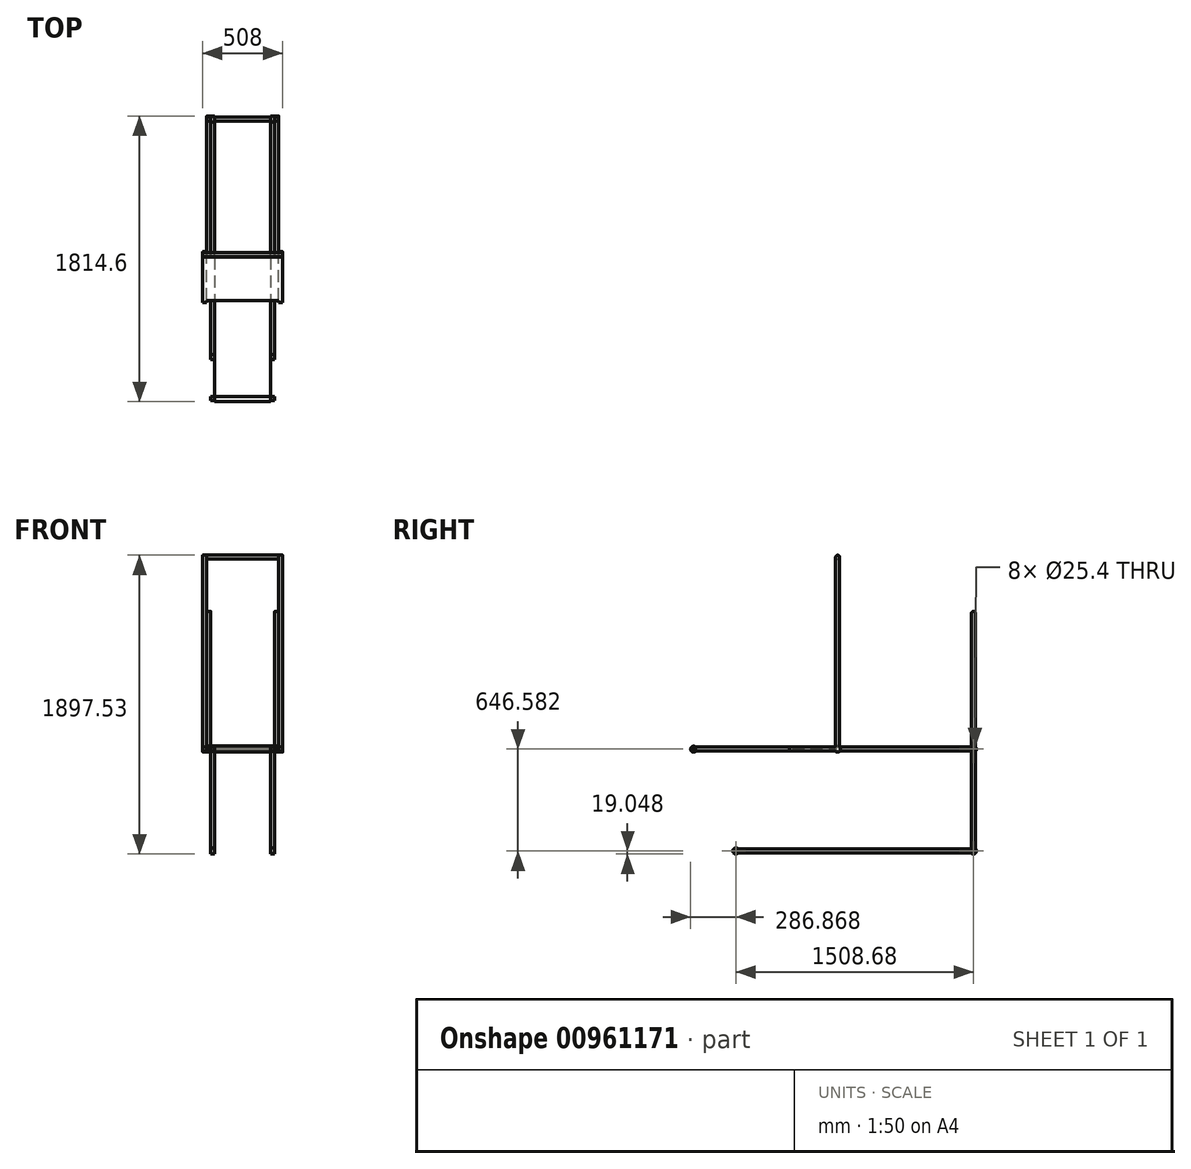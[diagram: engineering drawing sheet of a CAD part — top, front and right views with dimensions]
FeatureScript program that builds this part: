
annotation { "Feature Type Name" : "Feature", "Feature Type Description" : "" }
export const myFeature = defineFeature(function(context is Context, id is Id, definition is map)
    precondition{}
    {
        {
            var Q0;
            Q0=qCreatedBy(makeId("Right.planeOp"),FACE);
            var sketch = newSketch(context, id + "F0", { "sketchPlane" : qUnion([Q0])});
            skCircle(sketch, "E0", {"center": v(0, 0) * mm, "radius": 12.7 * mm});
            skLineSegment(sketch, "E1", {"start": v(12.7, 0) * mm, "end": v(12.7, 1219.2) * mm});
            skLineSegment(sketch, "E2", {"start": v(-12.7, 0) * mm, "end": v(-12.7, 1219.2) * mm});
            skLineSegment(sketch, "E3", {"start": v(0, -12.7) * mm, "end": v(-304.8, -12.7) * mm});
            skLineSegment(sketch, "E4", {"start": v(0, 12.7) * mm, "end": v(-304.8, 12.7) * mm});
            skLineSegment(sketch, "E5", {"start": v(-304.8, -12.7) * mm, "end": v(-304.8, 12.7) * mm});
            skLineSegment(sketch, "E6", {"start": v(-12.7, 1219.2) * mm, "end": v(12.7, 1219.2) * mm});
            skLineSegment(sketch, "E7", {"start": v(-304.8, 12.7) * mm, "end": v(-914.4, 12.7) * mm});
            skLineSegment(sketch, "E8", {"start": v(-304.8, -12.7) * mm, "end": v(-914.4, -12.7) * mm});
            skLineSegment(sketch, "E9", {"start": v(-914.4, -12.7) * mm, "end": v(-914.4, 12.7) * mm});
            skCircle(sketch, "E10", {"center": v(862.1, 0) * mm, "radius": 12.7 * mm});
            skLineSegment(sketch, "E11", {"start": v(0, -12.7) * mm, "end": v(862.1, -12.7) * mm});
            skLineSegment(sketch, "E12", {"start": v(862.1, 12.7) * mm, "end": v(0, 12.7) * mm});
            skLineSegment(sketch, "E13", {"start": v(874.8, 0) * mm, "end": v(874.8, 862.1) * mm});
            skLineSegment(sketch, "E14", {"start": v(849.4, 0) * mm, "end": v(849.4, 862.1) * mm});
            skCircle(sketch, "E15", {"center": v(-914.4, 0) * mm, "radius": 12.7 * mm});
            skLineSegment(sketch, "E16", {"start": v(849.4, 862.1) * mm, "end": v(874.8, 862.1) * mm});
            skCircle(sketch, "E17", {"center": v(862.1, 862.1) * mm, "radius": 12.7 * mm});
            skCircle(sketch, "E18", {"center": v(862.1, -646.58) * mm, "radius": 12.7 * mm});
            skLineSegment(sketch, "E19", {"start": v(849.4, -646.58) * mm, "end": v(849.4, 0) * mm});
            skLineSegment(sketch, "E20", {"start": v(874.8, -646.58) * mm, "end": v(874.8, 0) * mm});
            skCircle(sketch, "E21", {"center": v(-646.58, -646.58) * mm, "radius": 12.7 * mm});
            skLineSegment(sketch, "E22", {"start": v(-646.58, -659.28) * mm, "end": v(862.1, -659.28) * mm});
            skLineSegment(sketch, "E23", {"start": v(-646.58, -633.88) * mm, "end": v(862.1, -633.88) * mm});
            skCircle(sketch, "E24", {"center": v(0, 1219.2) * mm, "radius": 12.7 * mm});
            skCircle(sketch, "E25", {"center": v(0, 0) * mm, "radius": 19.05 * mm});
            skCircle(sketch, "E26", {"center": v(862.1, 0) * mm, "radius": 19.05 * mm});
            skCircle(sketch, "E27", {"center": v(862.1, -646.58) * mm, "radius": 19.05 * mm});
            skCircle(sketch, "E28", {"center": v(-914.4, 0) * mm, "radius": 19.05 * mm});
            skCircle(sketch, "E29", {"center": v(-646.58, -646.58) * mm, "radius": 19.05 * mm});
            skCircle(sketch, "E30", {"center": v(-304.8, 0) * mm, "radius": 12.7 * mm});
            skCircle(sketch, "E31", {"center": v(-304.8, 0) * mm, "radius": 19.05 * mm});
            skLineSegment(sketch, "E32.0", {"start": v(-17.96, -6.35) * mm, "end": v(-932.36, -6.35) * mm});
            skLineSegment(sketch, "E33.trimOffspring", {"start": v(-17.96, 6.35) * mm, "end": v(-932.36, 6.35) * mm});
            skSolve(sketch);
        }
        {
            var Q0;
            {var subQ1=sQuery(id+"F0.wireOp",EDGE,"E3");var subQ3=sQuery(id+"F0.wireOp",EDGE,"E25");var subQ4=makeQuery(id+"F0.imprint","INTERSECT",VERTEX,{"derivedFrom":[subQ1,subQ3]});Q0=makeQuery(id+"F0.imprint","IMPRINT",FACE,{"disambiguationData":[TD([[makeQuery(id+"F0.imprint","IMPRINT",EDGE,{"disambiguationData":[TD([[subQ4,-1.0]])],"derivedFrom":subQ3}),1.0]])]});}
            var Q1;
            {var subQ0=sQuery(id+"F0.wireOp",EDGE,"E6");Q1=makeQuery(id+"F0.imprint","IMPRINT",FACE,{"disambiguationData":[TD([[makeQuery(id+"F0.imprint","IMPRINT",EDGE,{"derivedFrom":subQ0}),-1.0]])]});}
            var Q2;
            {var subQ0=sQuery(id+"F0.wireOp",EDGE,"E2");var subQ1=sQuery(id+"F0.wireOp",EDGE,"E0");var subQ2=makeQuery(id+"F0.imprint","INTERSECT",VERTEX,{"derivedFrom":[subQ1,subQ0]});Q2=makeQuery(id+"F0.imprint","IMPRINT",FACE,{"disambiguationData":[TD([[makeQuery(id+"F0.imprint","IMPRINT",EDGE,{"disambiguationData":[TD([[subQ2,-1.0]])],"derivedFrom":subQ0}),-1.0]])]});}
            var Q3;
            {var subQ0=sQuery(id+"F0.wireOp",EDGE,"E1");var subQ1=sQuery(id+"F0.wireOp",EDGE,"E0");var subQ2=makeQuery(id+"F0.imprint","INTERSECT",VERTEX,{"derivedFrom":[subQ1,subQ0]});Q3=makeQuery(id+"F0.imprint","IMPRINT",FACE,{"disambiguationData":[TD([[makeQuery(id+"F0.imprint","IMPRINT",EDGE,{"disambiguationData":[TD([[subQ2,-1.0]])],"derivedFrom":subQ0}),1.0]])]});}
            var Q4;
            {var subQ3=sQuery(id+"F0.wireOp",EDGE,"E1");var subQ6=sQuery(id+"F0.wireOp",EDGE,"E0");var subQ9=makeQuery(id+"F0.imprint","INTERSECT",VERTEX,{"derivedFrom":[subQ6,subQ3]});Q4=makeQuery(id+"F0.imprint","IMPRINT",FACE,{"disambiguationData":[TD([[makeQuery(id+"F0.imprint","IMPRINT",EDGE,{"disambiguationData":[TD([[subQ9,-1.0]])],"derivedFrom":subQ3}),-1.0]])]});}
            var Q5;
            {var subQ0=sQuery(id+"F0.wireOp",EDGE,"E6");Q5=makeQuery(id+"F0.imprint","IMPRINT",FACE,{"disambiguationData":[TD([[makeQuery(id+"F0.imprint","IMPRINT",EDGE,{"derivedFrom":subQ0}),1.0]])]});}
            var Q6;
            {var subQ5=sQuery(id+"F0.wireOp",EDGE,"E25");var subQ7=sQuery(id+"F0.wireOp",EDGE,"E1");var subQ9=makeQuery(id+"F0.imprint","INTERSECT",VERTEX,{"derivedFrom":[subQ7,subQ5]});Q6=makeQuery(id+"F0.imprint","IMPRINT",FACE,{"disambiguationData":[TD([[makeQuery(id+"F0.imprint","IMPRINT",EDGE,{"disambiguationData":[TD([[subQ9,1.0]])],"derivedFrom":subQ7}),1.0]])]});}
            var Q7;
            {var subQ2=sQuery(id+"F0.wireOp",EDGE,"E1");var subQ4=sQuery(id+"F0.wireOp",EDGE,"E25");var subQ5=makeQuery(id+"F0.imprint","INTERSECT",VERTEX,{"derivedFrom":[subQ2,subQ4]});Q7=makeQuery(id+"F0.imprint","IMPRINT",FACE,{"disambiguationData":[TD([[makeQuery(id+"F0.imprint","IMPRINT",EDGE,{"disambiguationData":[TD([[subQ5,-1.0]])],"derivedFrom":subQ4}),-1.0]])]});}
            var Q8;
            {var subQ3=sQuery(id+"F0.wireOp",EDGE,"E2");var subQ5=sQuery(id+"F0.wireOp",EDGE,"E0");var subQ6=makeQuery(id+"F0.imprint","INTERSECT",VERTEX,{"derivedFrom":[subQ5,subQ3]});Q8=makeQuery(id+"F0.imprint","IMPRINT",FACE,{"disambiguationData":[TD([[makeQuery(id+"F0.imprint","IMPRINT",EDGE,{"disambiguationData":[TD([[subQ6,-1.0]])],"derivedFrom":subQ3}),1.0]])]});}
            var Q9;
            {var subQ0=sQuery(id+"F0.wireOp",EDGE,"E25");var subQ1=sQuery(id+"F0.wireOp",EDGE,"E1");var subQ2=makeQuery(id+"F0.imprint","INTERSECT",VERTEX,{"derivedFrom":[subQ1,subQ0]});Q9=makeQuery(id+"F0.imprint","IMPRINT",FACE,{"disambiguationData":[TD([[makeQuery(id+"F0.imprint","IMPRINT",EDGE,{"disambiguationData":[TD([[subQ2,1.0]])],"derivedFrom":subQ1}),-1.0]])]});}
            var Q10;
            {var subQ0=sQuery(id+"F0.wireOp",EDGE,"E25");var subQ1=sQuery(id+"F0.wireOp",EDGE,"E2");var subQ2=makeQuery(id+"F0.imprint","INTERSECT",VERTEX,{"derivedFrom":[subQ1,subQ0]});Q10=makeQuery(id+"F0.imprint","IMPRINT",FACE,{"disambiguationData":[TD([[makeQuery(id+"F0.imprint","IMPRINT",EDGE,{"disambiguationData":[TD([[subQ2,1.0]])],"derivedFrom":subQ1}),1.0]])]});}
            var Q11;
            {var subQ0=sQuery(id+"F0.wireOp",EDGE,"E25");var subQ1=sQuery(id+"F0.wireOp",EDGE,"E3");var subQ2=makeQuery(id+"F0.imprint","INTERSECT",VERTEX,{"derivedFrom":[subQ1,subQ0]});Q11=makeQuery(id+"F0.imprint","IMPRINT",FACE,{"disambiguationData":[TD([[makeQuery(id+"F0.imprint","IMPRINT",EDGE,{"disambiguationData":[TD([[subQ2,-1.0]])],"derivedFrom":subQ1}),-1.0]])]});}
            var Q12;
            {var subQ2=sQuery(id+"F0.wireOp",EDGE,"E3");var subQ4=sQuery(id+"F0.wireOp",EDGE,"E31");var subQ5=makeQuery(id+"F0.imprint","INTERSECT",VERTEX,{"derivedFrom":[subQ2,subQ4]});Q12=makeQuery(id+"F0.imprint","IMPRINT",FACE,{"disambiguationData":[TD([[makeQuery(id+"F0.imprint","IMPRINT",EDGE,{"disambiguationData":[TD([[subQ5,-1.0]])],"derivedFrom":subQ4}),1.0]])]});}
            var Q13;
            {var subQ1=sQuery(id+"F0.wireOp",EDGE,"E4");var subQ3=sQuery(id+"F0.wireOp",EDGE,"E31");var subQ4=makeQuery(id+"F0.imprint","INTERSECT",VERTEX,{"derivedFrom":[subQ1,subQ3]});Q13=makeQuery(id+"F0.imprint","IMPRINT",FACE,{"disambiguationData":[TD([[makeQuery(id+"F0.imprint","IMPRINT",EDGE,{"disambiguationData":[TD([[subQ4,1.0]])],"derivedFrom":subQ3}),1.0]])]});}
            var Q14;
            {var subQ0=sQuery(id+"F0.wireOp",EDGE,"E25");var subQ1=sQuery(id+"F0.wireOp",EDGE,"E4");var subQ2=makeQuery(id+"F0.imprint","INTERSECT",VERTEX,{"derivedFrom":[subQ1,subQ0]});Q14=makeQuery(id+"F0.imprint","IMPRINT",FACE,{"disambiguationData":[TD([[makeQuery(id+"F0.imprint","IMPRINT",EDGE,{"disambiguationData":[TD([[subQ2,-1.0]])],"derivedFrom":subQ1}),1.0]])]});}
            var Q15;
            {var subQ1=sQuery(id+"F0.wireOp",EDGE,"E5");var subQ3=sQuery(id+"F0.wireOp",EDGE,"E33.trimOffspring");var subQ4=makeQuery(id+"F0.imprint","INTERSECT",VERTEX,{"derivedFrom":[subQ1,subQ3]});Q15=makeQuery(id+"F0.imprint","IMPRINT",FACE,{"disambiguationData":[TD([[makeQuery(id+"F0.imprint","IMPRINT",EDGE,{"disambiguationData":[TD([[subQ4,1.0]])],"derivedFrom":subQ3}),-1.0]])]});}
            var Q16;
            {var subQ1=sQuery(id+"F0.wireOp",EDGE,"E5");var subQ3=sQuery(id+"F0.wireOp",EDGE,"E32.0");var subQ4=makeQuery(id+"F0.imprint","INTERSECT",VERTEX,{"derivedFrom":[subQ1,subQ3]});Q16=makeQuery(id+"F0.imprint","IMPRINT",FACE,{"disambiguationData":[TD([[makeQuery(id+"F0.imprint","IMPRINT",EDGE,{"disambiguationData":[TD([[subQ4,1.0]])],"derivedFrom":subQ3}),1.0]])]});}
            var Q17;
            {var subQ0=sQuery(id+"F0.wireOp",EDGE,"E32.0");var subQ1=sQuery(id+"F0.wireOp",EDGE,"E5");var subQ2=makeQuery(id+"F0.imprint","INTERSECT",VERTEX,{"derivedFrom":[subQ1,subQ0]});Q17=makeQuery(id+"F0.imprint","IMPRINT",FACE,{"disambiguationData":[TD([[makeQuery(id+"F0.imprint","IMPRINT",EDGE,{"disambiguationData":[TD([[subQ2,-1.0]])],"derivedFrom":subQ1}),-1.0]])]});}
            var Q18;
            {var subQ0=sQuery(id+"F0.wireOp",EDGE,"E32.0");var subQ1=sQuery(id+"F0.wireOp",EDGE,"E25");var subQ2=makeQuery(id+"F0.imprint","INTERSECT",VERTEX,{"derivedFrom":[subQ1,subQ0]});Q18=makeQuery(id+"F0.imprint","IMPRINT",FACE,{"disambiguationData":[TD([[makeQuery(id+"F0.imprint","IMPRINT",EDGE,{"disambiguationData":[TD([[subQ2,1.0]])],"derivedFrom":subQ1}),-1.0]])]});}
            var Q19;
            {var subQ0=sQuery(id+"F0.wireOp",EDGE,"E33.trimOffspring");var subQ1=sQuery(id+"F0.wireOp",EDGE,"E30");var subQ2=makeQuery(id+"F0.imprint","INTERSECT",VERTEX,{"disambiguationData":[OD(0.0)],"derivedFrom":[subQ1,subQ0]});Q19=makeQuery(id+"F0.imprint","IMPRINT",FACE,{"disambiguationData":[TD([[makeQuery(id+"F0.imprint","IMPRINT",EDGE,{"disambiguationData":[TD([[subQ2,1.0]])],"derivedFrom":subQ1}),-1.0]])]});}
            extrude(context, id + "F1", {"entities" : qUnion([Q0, Q1, Q2, Q3, Q4, Q5, Q6, Q7, Q8, Q9, Q10, Q11, Q12, Q13, Q14, Q15, Q16, Q17, Q18, Q19]), "depth" : 254 * mm, "offsetDistance" : 25.4 * mm, "hasSecondDirection" : true, "secondDirectionOppositeDirection" : false, "secondDirectionDepth" : 228.6 * mm});
        }
        {
            var Q0;
            {var subQ0=sQuery(id+"F0.wireOp",EDGE,"E6");Q0=makeQuery(id+"F0.imprint","IMPRINT",FACE,{"disambiguationData":[TD([[makeQuery(id+"F0.imprint","IMPRINT",EDGE,{"derivedFrom":subQ0}),-1.0]])]});}
            var Q1;
            {var subQ5=sQuery(id+"F0.wireOp",EDGE,"E25");var subQ7=sQuery(id+"F0.wireOp",EDGE,"E1");var subQ9=makeQuery(id+"F0.imprint","INTERSECT",VERTEX,{"derivedFrom":[subQ7,subQ5]});Q1=makeQuery(id+"F0.imprint","IMPRINT",FACE,{"disambiguationData":[TD([[makeQuery(id+"F0.imprint","IMPRINT",EDGE,{"disambiguationData":[TD([[subQ9,1.0]])],"derivedFrom":subQ7}),1.0]])]});}
            var Q2;
            {var subQ3=sQuery(id+"F0.wireOp",EDGE,"E2");var subQ5=sQuery(id+"F0.wireOp",EDGE,"E0");var subQ6=makeQuery(id+"F0.imprint","INTERSECT",VERTEX,{"derivedFrom":[subQ5,subQ3]});Q2=makeQuery(id+"F0.imprint","IMPRINT",FACE,{"disambiguationData":[TD([[makeQuery(id+"F0.imprint","IMPRINT",EDGE,{"disambiguationData":[TD([[subQ6,-1.0]])],"derivedFrom":subQ3}),1.0]])]});}
            var Q3;
            {var subQ0=sQuery(id+"F0.wireOp",EDGE,"E1");var subQ1=sQuery(id+"F0.wireOp",EDGE,"E0");var subQ2=makeQuery(id+"F0.imprint","INTERSECT",VERTEX,{"derivedFrom":[subQ1,subQ0]});Q3=makeQuery(id+"F0.imprint","IMPRINT",FACE,{"disambiguationData":[TD([[makeQuery(id+"F0.imprint","IMPRINT",EDGE,{"disambiguationData":[TD([[subQ2,-1.0]])],"derivedFrom":subQ0}),1.0]])]});}
            var Q4;
            {var subQ0=sQuery(id+"F0.wireOp",EDGE,"E6");Q4=makeQuery(id+"F0.imprint","IMPRINT",FACE,{"disambiguationData":[TD([[makeQuery(id+"F0.imprint","IMPRINT",EDGE,{"derivedFrom":subQ0}),1.0]])]});}
            var Q5;
            {var subQ3=sQuery(id+"F0.wireOp",EDGE,"E1");var subQ6=sQuery(id+"F0.wireOp",EDGE,"E0");var subQ9=makeQuery(id+"F0.imprint","INTERSECT",VERTEX,{"derivedFrom":[subQ6,subQ3]});Q5=makeQuery(id+"F0.imprint","IMPRINT",FACE,{"disambiguationData":[TD([[makeQuery(id+"F0.imprint","IMPRINT",EDGE,{"disambiguationData":[TD([[subQ9,-1.0]])],"derivedFrom":subQ3}),-1.0]])]});}
            var Q6;
            {var subQ2=sQuery(id+"F0.wireOp",EDGE,"E1");var subQ4=sQuery(id+"F0.wireOp",EDGE,"E25");var subQ5=makeQuery(id+"F0.imprint","INTERSECT",VERTEX,{"derivedFrom":[subQ2,subQ4]});Q6=makeQuery(id+"F0.imprint","IMPRINT",FACE,{"disambiguationData":[TD([[makeQuery(id+"F0.imprint","IMPRINT",EDGE,{"disambiguationData":[TD([[subQ5,-1.0]])],"derivedFrom":subQ4}),-1.0]])]});}
            var Q7;
            {var subQ0=sQuery(id+"F0.wireOp",EDGE,"E25");var subQ1=sQuery(id+"F0.wireOp",EDGE,"E1");var subQ2=makeQuery(id+"F0.imprint","INTERSECT",VERTEX,{"derivedFrom":[subQ1,subQ0]});Q7=makeQuery(id+"F0.imprint","IMPRINT",FACE,{"disambiguationData":[TD([[makeQuery(id+"F0.imprint","IMPRINT",EDGE,{"disambiguationData":[TD([[subQ2,1.0]])],"derivedFrom":subQ1}),-1.0]])]});}
            var Q8;
            {var subQ0=sQuery(id+"F0.wireOp",EDGE,"E2");var subQ1=sQuery(id+"F0.wireOp",EDGE,"E0");var subQ2=makeQuery(id+"F0.imprint","INTERSECT",VERTEX,{"derivedFrom":[subQ1,subQ0]});Q8=makeQuery(id+"F0.imprint","IMPRINT",FACE,{"disambiguationData":[TD([[makeQuery(id+"F0.imprint","IMPRINT",EDGE,{"disambiguationData":[TD([[subQ2,-1.0]])],"derivedFrom":subQ0}),-1.0]])]});}
            var Q9;
            {var subQ1=sQuery(id+"F0.wireOp",EDGE,"E3");var subQ3=sQuery(id+"F0.wireOp",EDGE,"E25");var subQ4=makeQuery(id+"F0.imprint","INTERSECT",VERTEX,{"derivedFrom":[subQ1,subQ3]});Q9=makeQuery(id+"F0.imprint","IMPRINT",FACE,{"disambiguationData":[TD([[makeQuery(id+"F0.imprint","IMPRINT",EDGE,{"disambiguationData":[TD([[subQ4,-1.0]])],"derivedFrom":subQ3}),1.0]])]});}
            var Q10;
            {var subQ0=sQuery(id+"F0.wireOp",EDGE,"E25");var subQ1=sQuery(id+"F0.wireOp",EDGE,"E2");var subQ2=makeQuery(id+"F0.imprint","INTERSECT",VERTEX,{"derivedFrom":[subQ1,subQ0]});Q10=makeQuery(id+"F0.imprint","IMPRINT",FACE,{"disambiguationData":[TD([[makeQuery(id+"F0.imprint","IMPRINT",EDGE,{"disambiguationData":[TD([[subQ2,1.0]])],"derivedFrom":subQ1}),1.0]])]});}
            var Q11;
            {var subQ0=sQuery(id+"F0.wireOp",EDGE,"E25");var subQ1=sQuery(id+"F0.wireOp",EDGE,"E3");var subQ2=makeQuery(id+"F0.imprint","INTERSECT",VERTEX,{"derivedFrom":[subQ1,subQ0]});Q11=makeQuery(id+"F0.imprint","IMPRINT",FACE,{"disambiguationData":[TD([[makeQuery(id+"F0.imprint","IMPRINT",EDGE,{"disambiguationData":[TD([[subQ2,-1.0]])],"derivedFrom":subQ1}),-1.0]])]});}
            var Q12;
            {var subQ2=sQuery(id+"F0.wireOp",EDGE,"E3");var subQ4=sQuery(id+"F0.wireOp",EDGE,"E31");var subQ5=makeQuery(id+"F0.imprint","INTERSECT",VERTEX,{"derivedFrom":[subQ2,subQ4]});Q12=makeQuery(id+"F0.imprint","IMPRINT",FACE,{"disambiguationData":[TD([[makeQuery(id+"F0.imprint","IMPRINT",EDGE,{"disambiguationData":[TD([[subQ5,-1.0]])],"derivedFrom":subQ4}),1.0]])]});}
            var Q13;
            {var subQ0=sQuery(id+"F0.wireOp",EDGE,"E25");var subQ1=sQuery(id+"F0.wireOp",EDGE,"E4");var subQ2=makeQuery(id+"F0.imprint","INTERSECT",VERTEX,{"derivedFrom":[subQ1,subQ0]});Q13=makeQuery(id+"F0.imprint","IMPRINT",FACE,{"disambiguationData":[TD([[makeQuery(id+"F0.imprint","IMPRINT",EDGE,{"disambiguationData":[TD([[subQ2,-1.0]])],"derivedFrom":subQ1}),1.0]])]});}
            var Q14;
            {var subQ1=sQuery(id+"F0.wireOp",EDGE,"E4");var subQ3=sQuery(id+"F0.wireOp",EDGE,"E31");var subQ4=makeQuery(id+"F0.imprint","INTERSECT",VERTEX,{"derivedFrom":[subQ1,subQ3]});Q14=makeQuery(id+"F0.imprint","IMPRINT",FACE,{"disambiguationData":[TD([[makeQuery(id+"F0.imprint","IMPRINT",EDGE,{"disambiguationData":[TD([[subQ4,1.0]])],"derivedFrom":subQ3}),1.0]])]});}
            var Q15;
            {var subQ1=sQuery(id+"F0.wireOp",EDGE,"E5");var subQ3=sQuery(id+"F0.wireOp",EDGE,"E33.trimOffspring");var subQ4=makeQuery(id+"F0.imprint","INTERSECT",VERTEX,{"derivedFrom":[subQ1,subQ3]});Q15=makeQuery(id+"F0.imprint","IMPRINT",FACE,{"disambiguationData":[TD([[makeQuery(id+"F0.imprint","IMPRINT",EDGE,{"disambiguationData":[TD([[subQ4,1.0]])],"derivedFrom":subQ3}),-1.0]])]});}
            var Q16;
            {var subQ0=sQuery(id+"F0.wireOp",EDGE,"E32.0");var subQ1=sQuery(id+"F0.wireOp",EDGE,"E5");var subQ2=makeQuery(id+"F0.imprint","INTERSECT",VERTEX,{"derivedFrom":[subQ1,subQ0]});Q16=makeQuery(id+"F0.imprint","IMPRINT",FACE,{"disambiguationData":[TD([[makeQuery(id+"F0.imprint","IMPRINT",EDGE,{"disambiguationData":[TD([[subQ2,-1.0]])],"derivedFrom":subQ1}),-1.0]])]});}
            var Q17;
            {var subQ1=sQuery(id+"F0.wireOp",EDGE,"E5");var subQ3=sQuery(id+"F0.wireOp",EDGE,"E32.0");var subQ4=makeQuery(id+"F0.imprint","INTERSECT",VERTEX,{"derivedFrom":[subQ1,subQ3]});Q17=makeQuery(id+"F0.imprint","IMPRINT",FACE,{"disambiguationData":[TD([[makeQuery(id+"F0.imprint","IMPRINT",EDGE,{"disambiguationData":[TD([[subQ4,1.0]])],"derivedFrom":subQ3}),1.0]])]});}
            var Q18;
            {var subQ0=sQuery(id+"F0.wireOp",EDGE,"E32.0");var subQ1=sQuery(id+"F0.wireOp",EDGE,"E25");var subQ2=makeQuery(id+"F0.imprint","INTERSECT",VERTEX,{"derivedFrom":[subQ1,subQ0]});Q18=makeQuery(id+"F0.imprint","IMPRINT",FACE,{"disambiguationData":[TD([[makeQuery(id+"F0.imprint","IMPRINT",EDGE,{"disambiguationData":[TD([[subQ2,1.0]])],"derivedFrom":subQ1}),-1.0]])]});}
            var Q19;
            {var subQ0=sQuery(id+"F0.wireOp",EDGE,"E33.trimOffspring");var subQ1=sQuery(id+"F0.wireOp",EDGE,"E30");var subQ2=makeQuery(id+"F0.imprint","INTERSECT",VERTEX,{"disambiguationData":[OD(0.0)],"derivedFrom":[subQ1,subQ0]});Q19=makeQuery(id+"F0.imprint","IMPRINT",FACE,{"disambiguationData":[TD([[makeQuery(id+"F0.imprint","IMPRINT",EDGE,{"disambiguationData":[TD([[subQ2,1.0]])],"derivedFrom":subQ1}),-1.0]])]});}
            extrude(context, id + "F2", {"entities" : qUnion([Q0, Q1, Q2, Q3, Q4, Q5, Q6, Q7, Q8, Q9, Q10, Q11, Q12, Q13, Q14, Q15, Q16, Q17, Q18, Q19]), "oppositeDirection" : true, "depth" : 254 * mm, "offsetDistance" : 25.4 * mm, "hasSecondDirection" : true, "secondDirectionOppositeDirection" : true, "secondDirectionDepth" : 228.6 * mm});
        }
        {
            var Q0;
            {var subQ0=sQuery(id+"F0.wireOp",EDGE,"E0");var subQ1=makeQuery(id+"F0.imprint","INTERSECT",VERTEX,{"derivedFrom":[subQ0,sQuery(id+"F0.wireOp",EDGE,"E1")]});Q0=makeQuery(id+"F0.imprint","IMPRINT",FACE,{"disambiguationData":[TD([[makeQuery(id+"F0.imprint","IMPRINT",EDGE,{"disambiguationData":[TD([[subQ1,-1.0]])],"derivedFrom":subQ0}),1.0]])]});}
            var Q1;
            {var subQ0=sQuery(id+"F0.wireOp",EDGE,"E6");Q1=makeQuery(id+"F0.imprint","IMPRINT",FACE,{"disambiguationData":[TD([[makeQuery(id+"F0.imprint","IMPRINT",EDGE,{"derivedFrom":subQ0}),-1.0]])]});}
            var Q2;
            {var subQ0=sQuery(id+"F0.wireOp",EDGE,"E6");Q2=makeQuery(id+"F0.imprint","IMPRINT",FACE,{"disambiguationData":[TD([[makeQuery(id+"F0.imprint","IMPRINT",EDGE,{"derivedFrom":subQ0}),1.0]])]});}
            var Q3;
            {var subQ0=sQuery(id+"F0.wireOp",EDGE,"E25");var subQ1=sQuery(id+"F0.wireOp",EDGE,"E4");var subQ2=makeQuery(id+"F0.imprint","INTERSECT",VERTEX,{"derivedFrom":[subQ1,subQ0]});Q3=makeQuery(id+"F0.imprint","IMPRINT",FACE,{"disambiguationData":[TD([[makeQuery(id+"F0.imprint","IMPRINT",EDGE,{"disambiguationData":[TD([[subQ2,-1.0]])],"derivedFrom":subQ1}),1.0]])]});}
            var Q4;
            {var subQ0=sQuery(id+"F0.wireOp",EDGE,"E25");var subQ1=sQuery(id+"F0.wireOp",EDGE,"E3");var subQ2=makeQuery(id+"F0.imprint","INTERSECT",VERTEX,{"derivedFrom":[subQ1,subQ0]});Q4=makeQuery(id+"F0.imprint","IMPRINT",FACE,{"disambiguationData":[TD([[makeQuery(id+"F0.imprint","IMPRINT",EDGE,{"disambiguationData":[TD([[subQ2,-1.0]])],"derivedFrom":subQ1}),-1.0]])]});}
            extrude(context, id + "F3", {"entities" : qUnion([Q0, Q1, Q2, Q3, Q4]), "operationType" : NewBodyOperationType.ADD, "depth" : 254 * mm, "offsetDistance" : 25.4 * mm, "hasSecondDirection" : true, "secondDirectionOppositeDirection" : true, "secondDirectionDepth" : 254 * mm});
        }
        {
            var Q0;
            {var subQ0=sQuery(id+"F0.wireOp",EDGE,"E1");var subQ1=sQuery(id+"F0.wireOp",EDGE,"E0");var subQ2=makeQuery(id+"F0.imprint","INTERSECT",VERTEX,{"derivedFrom":[subQ1,subQ0]});Q0=makeQuery(id+"F0.imprint","IMPRINT",FACE,{"disambiguationData":[TD([[makeQuery(id+"F0.imprint","IMPRINT",EDGE,{"disambiguationData":[TD([[subQ2,-1.0]])],"derivedFrom":subQ0}),1.0]])]});}
            var Q1;
            {var subQ0=sQuery(id+"F0.wireOp",EDGE,"E25");var subQ1=sQuery(id+"F0.wireOp",EDGE,"E1");var subQ2=makeQuery(id+"F0.imprint","INTERSECT",VERTEX,{"derivedFrom":[subQ1,subQ0]});Q1=makeQuery(id+"F0.imprint","IMPRINT",FACE,{"disambiguationData":[TD([[makeQuery(id+"F0.imprint","IMPRINT",EDGE,{"disambiguationData":[TD([[subQ2,1.0]])],"derivedFrom":subQ1}),-1.0]])]});}
            var Q2;
            {var subQ3=sQuery(id+"F0.wireOp",EDGE,"E1");var subQ6=sQuery(id+"F0.wireOp",EDGE,"E0");var subQ9=makeQuery(id+"F0.imprint","INTERSECT",VERTEX,{"derivedFrom":[subQ6,subQ3]});Q2=makeQuery(id+"F0.imprint","IMPRINT",FACE,{"disambiguationData":[TD([[makeQuery(id+"F0.imprint","IMPRINT",EDGE,{"disambiguationData":[TD([[subQ9,-1.0]])],"derivedFrom":subQ3}),-1.0]])]});}
            var Q3;
            {var subQ5=sQuery(id+"F0.wireOp",EDGE,"E25");var subQ7=sQuery(id+"F0.wireOp",EDGE,"E11");var subQ9=makeQuery(id+"F0.imprint","INTERSECT",VERTEX,{"derivedFrom":[subQ7,subQ5]});Q3=makeQuery(id+"F0.imprint","IMPRINT",FACE,{"disambiguationData":[TD([[makeQuery(id+"F0.imprint","IMPRINT",EDGE,{"disambiguationData":[TD([[subQ9,-1.0]])],"derivedFrom":subQ7}),1.0]])]});}
            var Q4;
            {var subQ0=sQuery(id+"F0.wireOp",EDGE,"E12");var subQ1=sQuery(id+"F0.wireOp",EDGE,"E10");var subQ2=makeQuery(id+"F0.imprint","INTERSECT",VERTEX,{"derivedFrom":[subQ1,subQ0]});Q4=makeQuery(id+"F0.imprint","IMPRINT",FACE,{"disambiguationData":[TD([[makeQuery(id+"F0.imprint","IMPRINT",EDGE,{"disambiguationData":[TD([[subQ2,-1.0]])],"derivedFrom":subQ0}),1.0]])]});}
            var Q5;
            {var subQ0=sQuery(id+"F0.wireOp",EDGE,"E11");var subQ1=sQuery(id+"F0.wireOp",EDGE,"E10");var subQ2=makeQuery(id+"F0.imprint","INTERSECT",VERTEX,{"derivedFrom":[subQ1,subQ0]});Q5=makeQuery(id+"F0.imprint","IMPRINT",FACE,{"disambiguationData":[TD([[makeQuery(id+"F0.imprint","IMPRINT",EDGE,{"disambiguationData":[TD([[subQ2,1.0]])],"derivedFrom":subQ0}),1.0]])]});}
            var Q6;
            {var subQ1=sQuery(id+"F0.wireOp",EDGE,"E3");var subQ3=sQuery(id+"F0.wireOp",EDGE,"E25");var subQ4=makeQuery(id+"F0.imprint","INTERSECT",VERTEX,{"derivedFrom":[subQ1,subQ3]});Q6=makeQuery(id+"F0.imprint","IMPRINT",FACE,{"disambiguationData":[TD([[makeQuery(id+"F0.imprint","IMPRINT",EDGE,{"disambiguationData":[TD([[subQ4,-1.0]])],"derivedFrom":subQ3}),1.0]])]});}
            var Q7;
            {var subQ5=sQuery(id+"F0.wireOp",EDGE,"E25");var subQ7=sQuery(id+"F0.wireOp",EDGE,"E1");var subQ9=makeQuery(id+"F0.imprint","INTERSECT",VERTEX,{"derivedFrom":[subQ7,subQ5]});Q7=makeQuery(id+"F0.imprint","IMPRINT",FACE,{"disambiguationData":[TD([[makeQuery(id+"F0.imprint","IMPRINT",EDGE,{"disambiguationData":[TD([[subQ9,1.0]])],"derivedFrom":subQ7}),1.0]])]});}
            var Q8;
            {var subQ5=sQuery(id+"F0.wireOp",EDGE,"E26");var subQ7=sQuery(id+"F0.wireOp",EDGE,"E11");var subQ9=makeQuery(id+"F0.imprint","INTERSECT",VERTEX,{"derivedFrom":[subQ7,subQ5]});Q8=makeQuery(id+"F0.imprint","IMPRINT",FACE,{"disambiguationData":[TD([[makeQuery(id+"F0.imprint","IMPRINT",EDGE,{"disambiguationData":[TD([[subQ9,-1.0]])],"derivedFrom":subQ7}),1.0]])]});}
            var Q9;
            {var subQ3=sQuery(id+"F0.wireOp",EDGE,"E12");var subQ6=sQuery(id+"F0.wireOp",EDGE,"E10");var subQ9=makeQuery(id+"F0.imprint","INTERSECT",VERTEX,{"derivedFrom":[subQ6,subQ3]});Q9=makeQuery(id+"F0.imprint","IMPRINT",FACE,{"disambiguationData":[TD([[makeQuery(id+"F0.imprint","IMPRINT",EDGE,{"disambiguationData":[TD([[subQ9,-1.0]])],"derivedFrom":subQ3}),-1.0]])]});}
            var Q10;
            {var subQ1=sQuery(id+"F0.wireOp",EDGE,"E13");var subQ3=sQuery(id+"F0.wireOp",EDGE,"E26");var subQ4=makeQuery(id+"F0.imprint","INTERSECT",VERTEX,{"derivedFrom":[subQ1,subQ3]});Q10=makeQuery(id+"F0.imprint","IMPRINT",FACE,{"disambiguationData":[TD([[makeQuery(id+"F0.imprint","IMPRINT",EDGE,{"disambiguationData":[TD([[subQ4,1.0]])],"derivedFrom":subQ3}),1.0]])]});}
            var Q11;
            {var subQ1=sQuery(id+"F0.wireOp",EDGE,"E10");var subQ7=sQuery(id+"F0.wireOp",EDGE,"E11");var subQ9=makeQuery(id+"F0.imprint","INTERSECT",VERTEX,{"derivedFrom":[subQ1,subQ7]});Q11=makeQuery(id+"F0.imprint","IMPRINT",FACE,{"disambiguationData":[TD([[makeQuery(id+"F0.imprint","IMPRINT",EDGE,{"disambiguationData":[TD([[subQ9,1.0]])],"derivedFrom":subQ7}),-1.0]])]});}
            var Q12;
            {var subQ0=sQuery(id+"F0.wireOp",EDGE,"E26");var subQ1=sQuery(id+"F0.wireOp",EDGE,"E12");var subQ2=makeQuery(id+"F0.imprint","INTERSECT",VERTEX,{"derivedFrom":[subQ1,subQ0]});Q12=makeQuery(id+"F0.imprint","IMPRINT",FACE,{"disambiguationData":[TD([[makeQuery(id+"F0.imprint","IMPRINT",EDGE,{"disambiguationData":[TD([[subQ2,1.0]])],"derivedFrom":subQ1}),-1.0]])]});}
            var Q13;
            {var subQ0=sQuery(id+"F0.wireOp",EDGE,"E26");var subQ1=sQuery(id+"F0.wireOp",EDGE,"E11");var subQ2=makeQuery(id+"F0.imprint","INTERSECT",VERTEX,{"derivedFrom":[subQ1,subQ0]});Q13=makeQuery(id+"F0.imprint","IMPRINT",FACE,{"disambiguationData":[TD([[makeQuery(id+"F0.imprint","IMPRINT",EDGE,{"disambiguationData":[TD([[subQ2,-1.0]])],"derivedFrom":subQ1}),-1.0]])]});}
            var Q14;
            {var subQ2=sQuery(id+"F0.wireOp",EDGE,"E13");var subQ4=sQuery(id+"F0.wireOp",EDGE,"E26");var subQ5=makeQuery(id+"F0.imprint","INTERSECT",VERTEX,{"derivedFrom":[subQ2,subQ4]});Q14=makeQuery(id+"F0.imprint","IMPRINT",FACE,{"disambiguationData":[TD([[makeQuery(id+"F0.imprint","IMPRINT",EDGE,{"disambiguationData":[TD([[subQ5,-1.0]])],"derivedFrom":subQ4}),-1.0]])]});}
            var Q15;
            {var subQ0=sQuery(id+"F0.wireOp",EDGE,"E16");Q15=makeQuery(id+"F0.imprint","IMPRINT",FACE,{"disambiguationData":[TD([[makeQuery(id+"F0.imprint","IMPRINT",EDGE,{"derivedFrom":subQ0}),-1.0]])]});}
            var Q16;
            {var subQ0=sQuery(id+"F0.wireOp",EDGE,"E16");Q16=makeQuery(id+"F0.imprint","IMPRINT",FACE,{"disambiguationData":[TD([[makeQuery(id+"F0.imprint","IMPRINT",EDGE,{"derivedFrom":subQ0}),1.0]])]});}
            extrude(context, id + "F4", {"entities" : qUnion([Q0, Q1, Q2, Q3, Q4, Q5, Q6, Q7, Q8, Q9, Q10, Q11, Q12, Q13, Q14, Q15, Q16]), "depth" : 228.6 * mm, "offsetDistance" : 25.4 * mm, "hasSecondDirection" : true, "secondDirectionOppositeDirection" : false, "secondDirectionDepth" : 203.2 * mm});
        }
        {
            var Q0;
            {var subQ5=sQuery(id+"F0.wireOp",EDGE,"E26");var subQ7=sQuery(id+"F0.wireOp",EDGE,"E11");var subQ9=makeQuery(id+"F0.imprint","INTERSECT",VERTEX,{"derivedFrom":[subQ7,subQ5]});Q0=makeQuery(id+"F0.imprint","IMPRINT",FACE,{"disambiguationData":[TD([[makeQuery(id+"F0.imprint","IMPRINT",EDGE,{"disambiguationData":[TD([[subQ9,-1.0]])],"derivedFrom":subQ7}),1.0]])]});}
            var Q1;
            {var subQ0=sQuery(id+"F0.wireOp",EDGE,"E26");var subQ1=sQuery(id+"F0.wireOp",EDGE,"E12");var subQ2=makeQuery(id+"F0.imprint","INTERSECT",VERTEX,{"derivedFrom":[subQ1,subQ0]});Q1=makeQuery(id+"F0.imprint","IMPRINT",FACE,{"disambiguationData":[TD([[makeQuery(id+"F0.imprint","IMPRINT",EDGE,{"disambiguationData":[TD([[subQ2,1.0]])],"derivedFrom":subQ1}),-1.0]])]});}
            var Q2;
            {var subQ0=sQuery(id+"F0.wireOp",EDGE,"E26");var subQ1=sQuery(id+"F0.wireOp",EDGE,"E11");var subQ2=makeQuery(id+"F0.imprint","INTERSECT",VERTEX,{"derivedFrom":[subQ1,subQ0]});Q2=makeQuery(id+"F0.imprint","IMPRINT",FACE,{"disambiguationData":[TD([[makeQuery(id+"F0.imprint","IMPRINT",EDGE,{"disambiguationData":[TD([[subQ2,-1.0]])],"derivedFrom":subQ1}),-1.0]])]});}
            var Q3;
            {var subQ0=sQuery(id+"F0.wireOp",EDGE,"E25");var subQ1=sQuery(id+"F0.wireOp",EDGE,"E1");var subQ2=makeQuery(id+"F0.imprint","INTERSECT",VERTEX,{"derivedFrom":[subQ1,subQ0]});Q3=makeQuery(id+"F0.imprint","IMPRINT",FACE,{"disambiguationData":[TD([[makeQuery(id+"F0.imprint","IMPRINT",EDGE,{"disambiguationData":[TD([[subQ2,1.0]])],"derivedFrom":subQ1}),-1.0]])]});}
            var Q4;
            {var subQ1=sQuery(id+"F0.wireOp",EDGE,"E13");var subQ3=sQuery(id+"F0.wireOp",EDGE,"E26");var subQ4=makeQuery(id+"F0.imprint","INTERSECT",VERTEX,{"derivedFrom":[subQ1,subQ3]});Q4=makeQuery(id+"F0.imprint","IMPRINT",FACE,{"disambiguationData":[TD([[makeQuery(id+"F0.imprint","IMPRINT",EDGE,{"disambiguationData":[TD([[subQ4,1.0]])],"derivedFrom":subQ3}),1.0]])]});}
            var Q5;
            {var subQ3=sQuery(id+"F0.wireOp",EDGE,"E1");var subQ5=sQuery(id+"F0.wireOp",EDGE,"E25");var subQ6=makeQuery(id+"F0.imprint","INTERSECT",VERTEX,{"derivedFrom":[subQ3,subQ5]});Q5=makeQuery(id+"F0.imprint","IMPRINT",FACE,{"disambiguationData":[TD([[makeQuery(id+"F0.imprint","IMPRINT",EDGE,{"disambiguationData":[TD([[subQ6,1.0]])],"derivedFrom":subQ3}),1.0]])]});}
            var Q6;
            {var subQ0=sQuery(id+"F0.wireOp",EDGE,"E12");var subQ1=sQuery(id+"F0.wireOp",EDGE,"E10");var subQ2=makeQuery(id+"F0.imprint","INTERSECT",VERTEX,{"derivedFrom":[subQ1,subQ0]});Q6=makeQuery(id+"F0.imprint","IMPRINT",FACE,{"disambiguationData":[TD([[makeQuery(id+"F0.imprint","IMPRINT",EDGE,{"disambiguationData":[TD([[subQ2,-1.0]])],"derivedFrom":subQ0}),1.0]])]});}
            var Q7;
            {var subQ3=sQuery(id+"F0.wireOp",EDGE,"E1");var subQ6=sQuery(id+"F0.wireOp",EDGE,"E0");var subQ9=makeQuery(id+"F0.imprint","INTERSECT",VERTEX,{"derivedFrom":[subQ6,subQ3]});Q7=makeQuery(id+"F0.imprint","IMPRINT",FACE,{"disambiguationData":[TD([[makeQuery(id+"F0.imprint","IMPRINT",EDGE,{"disambiguationData":[TD([[subQ9,-1.0]])],"derivedFrom":subQ3}),-1.0]])]});}
            var Q8;
            {var subQ3=sQuery(id+"F0.wireOp",EDGE,"E12");var subQ6=sQuery(id+"F0.wireOp",EDGE,"E10");var subQ9=makeQuery(id+"F0.imprint","INTERSECT",VERTEX,{"derivedFrom":[subQ6,subQ3]});Q8=makeQuery(id+"F0.imprint","IMPRINT",FACE,{"disambiguationData":[TD([[makeQuery(id+"F0.imprint","IMPRINT",EDGE,{"disambiguationData":[TD([[subQ9,-1.0]])],"derivedFrom":subQ3}),-1.0]])]});}
            var Q9;
            {var subQ1=sQuery(id+"F0.wireOp",EDGE,"E10");var subQ7=sQuery(id+"F0.wireOp",EDGE,"E11");var subQ9=makeQuery(id+"F0.imprint","INTERSECT",VERTEX,{"derivedFrom":[subQ1,subQ7]});Q9=makeQuery(id+"F0.imprint","IMPRINT",FACE,{"disambiguationData":[TD([[makeQuery(id+"F0.imprint","IMPRINT",EDGE,{"disambiguationData":[TD([[subQ9,1.0]])],"derivedFrom":subQ7}),-1.0]])]});}
            var Q10;
            {var subQ0=sQuery(id+"F0.wireOp",EDGE,"E1");var subQ1=sQuery(id+"F0.wireOp",EDGE,"E0");var subQ2=makeQuery(id+"F0.imprint","INTERSECT",VERTEX,{"derivedFrom":[subQ1,subQ0]});Q10=makeQuery(id+"F0.imprint","IMPRINT",FACE,{"disambiguationData":[TD([[makeQuery(id+"F0.imprint","IMPRINT",EDGE,{"disambiguationData":[TD([[subQ2,-1.0]])],"derivedFrom":subQ0}),1.0]])]});}
            var Q11;
            {var subQ0=sQuery(id+"F0.wireOp",EDGE,"E11");var subQ1=sQuery(id+"F0.wireOp",EDGE,"E10");var subQ2=makeQuery(id+"F0.imprint","INTERSECT",VERTEX,{"derivedFrom":[subQ1,subQ0]});Q11=makeQuery(id+"F0.imprint","IMPRINT",FACE,{"disambiguationData":[TD([[makeQuery(id+"F0.imprint","IMPRINT",EDGE,{"disambiguationData":[TD([[subQ2,1.0]])],"derivedFrom":subQ0}),1.0]])]});}
            var Q12;
            {var subQ0=sQuery(id+"F0.wireOp",EDGE,"E25");var subQ1=sQuery(id+"F0.wireOp",EDGE,"E11");var subQ2=makeQuery(id+"F0.imprint","INTERSECT",VERTEX,{"derivedFrom":[subQ1,subQ0]});Q12=makeQuery(id+"F0.imprint","IMPRINT",FACE,{"disambiguationData":[TD([[makeQuery(id+"F0.imprint","IMPRINT",EDGE,{"disambiguationData":[TD([[subQ2,-1.0]])],"derivedFrom":subQ1}),1.0]])]});}
            var Q13;
            {var subQ1=sQuery(id+"F0.wireOp",EDGE,"E3");var subQ3=sQuery(id+"F0.wireOp",EDGE,"E25");var subQ4=makeQuery(id+"F0.imprint","INTERSECT",VERTEX,{"derivedFrom":[subQ1,subQ3]});Q13=makeQuery(id+"F0.imprint","IMPRINT",FACE,{"disambiguationData":[TD([[makeQuery(id+"F0.imprint","IMPRINT",EDGE,{"disambiguationData":[TD([[subQ4,-1.0]])],"derivedFrom":subQ3}),1.0]])]});}
            var Q14;
            {var subQ2=sQuery(id+"F0.wireOp",EDGE,"E13");var subQ4=sQuery(id+"F0.wireOp",EDGE,"E26");var subQ5=makeQuery(id+"F0.imprint","INTERSECT",VERTEX,{"derivedFrom":[subQ2,subQ4]});Q14=makeQuery(id+"F0.imprint","IMPRINT",FACE,{"disambiguationData":[TD([[makeQuery(id+"F0.imprint","IMPRINT",EDGE,{"disambiguationData":[TD([[subQ5,-1.0]])],"derivedFrom":subQ4}),-1.0]])]});}
            var Q15;
            {var subQ0=sQuery(id+"F0.wireOp",EDGE,"E16");Q15=makeQuery(id+"F0.imprint","IMPRINT",FACE,{"disambiguationData":[TD([[makeQuery(id+"F0.imprint","IMPRINT",EDGE,{"derivedFrom":subQ0}),-1.0]])]});}
            var Q16;
            {var subQ0=sQuery(id+"F0.wireOp",EDGE,"E16");Q16=makeQuery(id+"F0.imprint","IMPRINT",FACE,{"disambiguationData":[TD([[makeQuery(id+"F0.imprint","IMPRINT",EDGE,{"derivedFrom":subQ0}),1.0]])]});}
            extrude(context, id + "F5", {"entities" : qUnion([Q0, Q1, Q2, Q3, Q4, Q5, Q6, Q7, Q8, Q9, Q10, Q11, Q12, Q13, Q14, Q15, Q16]), "oppositeDirection" : true, "depth" : 228.6 * mm, "offsetDistance" : 25.4 * mm, "hasSecondDirection" : true, "secondDirectionOppositeDirection" : true, "secondDirectionDepth" : 203.2 * mm});
        }
        {
            var Q0;
            {var subQ0=sQuery(id+"F0.wireOp",EDGE,"E12");var subQ1=sQuery(id+"F0.wireOp",EDGE,"E10");var subQ2=makeQuery(id+"F0.imprint","INTERSECT",VERTEX,{"derivedFrom":[subQ1,subQ0]});Q0=makeQuery(id+"F0.imprint","IMPRINT",FACE,{"disambiguationData":[TD([[makeQuery(id+"F0.imprint","IMPRINT",EDGE,{"disambiguationData":[TD([[subQ2,-1.0]])],"derivedFrom":subQ0}),1.0]])]});}
            var Q1;
            {var subQ0=sQuery(id+"F0.wireOp",EDGE,"E19");var subQ1=sQuery(id+"F0.wireOp",EDGE,"E18");var subQ2=makeQuery(id+"F0.imprint","INTERSECT",VERTEX,{"derivedFrom":[subQ1,subQ0]});Q1=makeQuery(id+"F0.imprint","IMPRINT",FACE,{"disambiguationData":[TD([[makeQuery(id+"F0.imprint","IMPRINT",EDGE,{"disambiguationData":[TD([[subQ2,1.0]])],"derivedFrom":subQ1}),-1.0]])]});}
            var Q2;
            {var subQ0=sQuery(id+"F0.wireOp",EDGE,"E27");var subQ1=sQuery(id+"F0.wireOp",EDGE,"E19");var subQ2=makeQuery(id+"F0.imprint","INTERSECT",VERTEX,{"derivedFrom":[subQ1,subQ0]});Q2=makeQuery(id+"F0.imprint","IMPRINT",FACE,{"disambiguationData":[TD([[makeQuery(id+"F0.imprint","IMPRINT",EDGE,{"disambiguationData":[TD([[subQ2,-1.0]])],"derivedFrom":subQ1}),-1.0]])]});}
            var Q3;
            {var subQ1=sQuery(id+"F0.wireOp",EDGE,"E13");var subQ3=sQuery(id+"F0.wireOp",EDGE,"E26");var subQ4=makeQuery(id+"F0.imprint","INTERSECT",VERTEX,{"derivedFrom":[subQ1,subQ3]});Q3=makeQuery(id+"F0.imprint","IMPRINT",FACE,{"disambiguationData":[TD([[makeQuery(id+"F0.imprint","IMPRINT",EDGE,{"disambiguationData":[TD([[subQ4,1.0]])],"derivedFrom":subQ3}),1.0]])]});}
            var Q4;
            {var subQ0=sQuery(id+"F0.wireOp",EDGE,"E26");var subQ1=sQuery(id+"F0.wireOp",EDGE,"E11");var subQ2=makeQuery(id+"F0.imprint","INTERSECT",VERTEX,{"derivedFrom":[subQ1,subQ0]});Q4=makeQuery(id+"F0.imprint","IMPRINT",FACE,{"disambiguationData":[TD([[makeQuery(id+"F0.imprint","IMPRINT",EDGE,{"disambiguationData":[TD([[subQ2,-1.0]])],"derivedFrom":subQ1}),-1.0]])]});}
            var Q5;
            {var subQ1=sQuery(id+"F0.wireOp",EDGE,"E18");var subQ5=sQuery(id+"F0.wireOp",EDGE,"E19");var subQ6=makeQuery(id+"F0.imprint","INTERSECT",VERTEX,{"derivedFrom":[subQ1,subQ5]});Q5=makeQuery(id+"F0.imprint","IMPRINT",FACE,{"disambiguationData":[TD([[makeQuery(id+"F0.imprint","IMPRINT",EDGE,{"disambiguationData":[TD([[subQ6,-1.0]])],"derivedFrom":subQ1}),-1.0]])]});}
            var Q6;
            {var subQ1=sQuery(id+"F0.wireOp",EDGE,"E10");var subQ7=sQuery(id+"F0.wireOp",EDGE,"E11");var subQ9=makeQuery(id+"F0.imprint","INTERSECT",VERTEX,{"derivedFrom":[subQ1,subQ7]});Q6=makeQuery(id+"F0.imprint","IMPRINT",FACE,{"disambiguationData":[TD([[makeQuery(id+"F0.imprint","IMPRINT",EDGE,{"disambiguationData":[TD([[subQ9,1.0]])],"derivedFrom":subQ7}),-1.0]])]});}
            var Q7;
            {var subQ0=sQuery(id+"F0.wireOp",EDGE,"E26");var subQ1=sQuery(id+"F0.wireOp",EDGE,"E12");var subQ2=makeQuery(id+"F0.imprint","INTERSECT",VERTEX,{"derivedFrom":[subQ1,subQ0]});Q7=makeQuery(id+"F0.imprint","IMPRINT",FACE,{"disambiguationData":[TD([[makeQuery(id+"F0.imprint","IMPRINT",EDGE,{"disambiguationData":[TD([[subQ2,1.0]])],"derivedFrom":subQ1}),-1.0]])]});}
            var Q8;
            {var subQ1=sQuery(id+"F0.wireOp",EDGE,"E18");var subQ5=sQuery(id+"F0.wireOp",EDGE,"E20");var subQ6=makeQuery(id+"F0.imprint","INTERSECT",VERTEX,{"derivedFrom":[subQ1,subQ5]});Q8=makeQuery(id+"F0.imprint","IMPRINT",FACE,{"disambiguationData":[TD([[makeQuery(id+"F0.imprint","IMPRINT",EDGE,{"disambiguationData":[TD([[subQ6,-1.0]])],"derivedFrom":subQ1}),-1.0]])]});}
            var Q9;
            {var subQ5=sQuery(id+"F0.wireOp",EDGE,"E26");var subQ7=sQuery(id+"F0.wireOp",EDGE,"E11");var subQ9=makeQuery(id+"F0.imprint","INTERSECT",VERTEX,{"derivedFrom":[subQ7,subQ5]});Q9=makeQuery(id+"F0.imprint","IMPRINT",FACE,{"disambiguationData":[TD([[makeQuery(id+"F0.imprint","IMPRINT",EDGE,{"disambiguationData":[TD([[subQ9,-1.0]])],"derivedFrom":subQ7}),1.0]])]});}
            var Q10;
            {var subQ0=sQuery(id+"F0.wireOp",EDGE,"E11");var subQ1=sQuery(id+"F0.wireOp",EDGE,"E10");var subQ2=makeQuery(id+"F0.imprint","INTERSECT",VERTEX,{"derivedFrom":[subQ1,subQ0]});Q10=makeQuery(id+"F0.imprint","IMPRINT",FACE,{"disambiguationData":[TD([[makeQuery(id+"F0.imprint","IMPRINT",EDGE,{"disambiguationData":[TD([[subQ2,1.0]])],"derivedFrom":subQ0}),1.0]])]});}
            var Q11;
            {var subQ3=sQuery(id+"F0.wireOp",EDGE,"E12");var subQ6=sQuery(id+"F0.wireOp",EDGE,"E10");var subQ9=makeQuery(id+"F0.imprint","INTERSECT",VERTEX,{"derivedFrom":[subQ6,subQ3]});Q11=makeQuery(id+"F0.imprint","IMPRINT",FACE,{"disambiguationData":[TD([[makeQuery(id+"F0.imprint","IMPRINT",EDGE,{"disambiguationData":[TD([[subQ9,-1.0]])],"derivedFrom":subQ3}),-1.0]])]});}
            var Q12;
            {var subQ0=sQuery(id+"F0.wireOp",EDGE,"E27");var subQ1=sQuery(id+"F0.wireOp",EDGE,"E19");var subQ2=makeQuery(id+"F0.imprint","INTERSECT",VERTEX,{"derivedFrom":[subQ1,subQ0]});Q12=makeQuery(id+"F0.imprint","IMPRINT",FACE,{"disambiguationData":[TD([[makeQuery(id+"F0.imprint","IMPRINT",EDGE,{"disambiguationData":[TD([[subQ2,1.0]])],"derivedFrom":subQ1}),1.0]])]});}
            var Q13;
            {var subQ0=sQuery(id+"F0.wireOp",EDGE,"E20");var subQ1=sQuery(id+"F0.wireOp",EDGE,"E18");var subQ2=makeQuery(id+"F0.imprint","INTERSECT",VERTEX,{"derivedFrom":[subQ1,subQ0]});Q13=makeQuery(id+"F0.imprint","IMPRINT",FACE,{"disambiguationData":[TD([[makeQuery(id+"F0.imprint","IMPRINT",EDGE,{"disambiguationData":[TD([[subQ2,1.0]])],"derivedFrom":subQ1}),-1.0]])]});}
            var Q14;
            {var subQ0=sQuery(id+"F0.wireOp",EDGE,"E29");var subQ1=sQuery(id+"F0.wireOp",EDGE,"E22");var subQ2=makeQuery(id+"F0.imprint","INTERSECT",VERTEX,{"derivedFrom":[subQ1,subQ0]});Q14=makeQuery(id+"F0.imprint","IMPRINT",FACE,{"disambiguationData":[TD([[makeQuery(id+"F0.imprint","IMPRINT",EDGE,{"disambiguationData":[TD([[subQ2,-1.0]])],"derivedFrom":subQ1}),1.0]])]});}
            var Q15;
            {var subQ0=sQuery(id+"F0.wireOp",EDGE,"E22");var subQ1=sQuery(id+"F0.wireOp",EDGE,"E21");var subQ2=makeQuery(id+"F0.imprint","INTERSECT",VERTEX,{"derivedFrom":[subQ1,subQ0]});Q15=makeQuery(id+"F0.imprint","IMPRINT",FACE,{"disambiguationData":[TD([[makeQuery(id+"F0.imprint","IMPRINT",EDGE,{"disambiguationData":[TD([[subQ2,-1.0]])],"derivedFrom":subQ1}),-1.0]])]});}
            var Q16;
            {var subQ0=sQuery(id+"F0.wireOp",EDGE,"E22");var subQ1=sQuery(id+"F0.wireOp",EDGE,"E21");var subQ2=makeQuery(id+"F0.imprint","INTERSECT",VERTEX,{"derivedFrom":[subQ1,subQ0]});Q16=makeQuery(id+"F0.imprint","IMPRINT",FACE,{"disambiguationData":[TD([[makeQuery(id+"F0.imprint","IMPRINT",EDGE,{"disambiguationData":[TD([[subQ2,1.0]])],"derivedFrom":subQ1}),-1.0]])]});}
            extrude(context, id + "F6", {"entities" : qUnion([Q0, Q1, Q2, Q3, Q4, Q5, Q6, Q7, Q8, Q9, Q10, Q11, Q12, Q13, Q14, Q15, Q16]), "depth" : 203.2 * mm, "offsetDistance" : 25.4 * mm, "hasSecondDirection" : true, "secondDirectionOppositeDirection" : false, "secondDirectionDepth" : 177.8 * mm});
        }
        {
            var Q0;
            {var subQ0=sQuery(id+"F0.wireOp",EDGE,"E10");var subQ1=makeQuery(id+"F0.imprint","INTERSECT",VERTEX,{"derivedFrom":[subQ0,sQuery(id+"F0.wireOp",EDGE,"E12")]});Q0=makeQuery(id+"F0.imprint","IMPRINT",FACE,{"disambiguationData":[TD([[makeQuery(id+"F0.imprint","IMPRINT",EDGE,{"disambiguationData":[TD([[subQ1,1.0]])],"derivedFrom":subQ0}),1.0]])]});}
            extrude(context, id + "F7", {"entities" : qUnion([Q0]), "endBound" : BoundingType.SYMMETRIC, "depth" : 457.2 * mm, "offsetDistance" : 25.4 * mm});
        }
        {
            var Q0;
            {var subQ1=sQuery(id+"F0.wireOp",EDGE,"E5");var subQ3=sQuery(id+"F0.wireOp",EDGE,"E33.trimOffspring");var subQ4=makeQuery(id+"F0.imprint","INTERSECT",VERTEX,{"derivedFrom":[subQ1,subQ3]});Q0=makeQuery(id+"F0.imprint","IMPRINT",FACE,{"disambiguationData":[TD([[makeQuery(id+"F0.imprint","IMPRINT",EDGE,{"disambiguationData":[TD([[subQ4,1.0]])],"derivedFrom":subQ3}),-1.0]])]});}
            var Q1;
            {var subQ3=sQuery(id+"F0.wireOp",EDGE,"E28");var subQ5=sQuery(id+"F0.wireOp",EDGE,"E33.trimOffspring");var subQ7=makeQuery(id+"F0.imprint","INTERSECT",VERTEX,{"disambiguationData":[OD(0.0)],"derivedFrom":[subQ3,subQ5]});Q1=makeQuery(id+"F0.imprint","IMPRINT",FACE,{"disambiguationData":[TD([[makeQuery(id+"F0.imprint","IMPRINT",EDGE,{"disambiguationData":[TD([[subQ7,1.0]])],"derivedFrom":subQ3}),1.0]])]});}
            var Q2;
            {var subQ1=sQuery(id+"F0.wireOp",EDGE,"E5");var subQ3=sQuery(id+"F0.wireOp",EDGE,"E32.0");var subQ4=makeQuery(id+"F0.imprint","INTERSECT",VERTEX,{"derivedFrom":[subQ1,subQ3]});Q2=makeQuery(id+"F0.imprint","IMPRINT",FACE,{"disambiguationData":[TD([[makeQuery(id+"F0.imprint","IMPRINT",EDGE,{"disambiguationData":[TD([[subQ4,-1.0]])],"derivedFrom":subQ3}),1.0]])]});}
            var Q3;
            {var subQ0=sQuery(id+"F0.wireOp",EDGE,"E31");var subQ1=sQuery(id+"F0.wireOp",EDGE,"E8");var subQ2=makeQuery(id+"F0.imprint","INTERSECT",VERTEX,{"derivedFrom":[subQ1,subQ0]});Q3=makeQuery(id+"F0.imprint","IMPRINT",FACE,{"disambiguationData":[TD([[makeQuery(id+"F0.imprint","IMPRINT",EDGE,{"disambiguationData":[TD([[subQ2,-1.0]])],"derivedFrom":subQ1}),-1.0]])]});}
            var Q4;
            {var subQ0=sQuery(id+"F0.wireOp",EDGE,"E32.0");var subQ1=sQuery(id+"F0.wireOp",EDGE,"E5");var subQ2=makeQuery(id+"F0.imprint","INTERSECT",VERTEX,{"derivedFrom":[subQ1,subQ0]});Q4=makeQuery(id+"F0.imprint","IMPRINT",FACE,{"disambiguationData":[TD([[makeQuery(id+"F0.imprint","IMPRINT",EDGE,{"disambiguationData":[TD([[subQ2,-1.0]])],"derivedFrom":subQ1}),-1.0]])]});}
            var Q5;
            {var subQ0=sQuery(id+"F0.wireOp",EDGE,"E32.0");var subQ1=sQuery(id+"F0.wireOp",EDGE,"E5");var subQ2=makeQuery(id+"F0.imprint","INTERSECT",VERTEX,{"derivedFrom":[subQ1,subQ0]});Q5=makeQuery(id+"F0.imprint","IMPRINT",FACE,{"disambiguationData":[TD([[makeQuery(id+"F0.imprint","IMPRINT",EDGE,{"disambiguationData":[TD([[subQ2,-1.0]])],"derivedFrom":subQ1}),1.0]])]});}
            var Q6;
            {var subQ0=sQuery(id+"F0.wireOp",EDGE,"E31");var subQ1=sQuery(id+"F0.wireOp",EDGE,"E7");var subQ2=makeQuery(id+"F0.imprint","INTERSECT",VERTEX,{"derivedFrom":[subQ1,subQ0]});Q6=makeQuery(id+"F0.imprint","IMPRINT",FACE,{"disambiguationData":[TD([[makeQuery(id+"F0.imprint","IMPRINT",EDGE,{"disambiguationData":[TD([[subQ2,-1.0]])],"derivedFrom":subQ1}),1.0]])]});}
            var Q7;
            {var subQ1=sQuery(id+"F0.wireOp",EDGE,"E4");var subQ3=sQuery(id+"F0.wireOp",EDGE,"E31");var subQ4=makeQuery(id+"F0.imprint","INTERSECT",VERTEX,{"derivedFrom":[subQ1,subQ3]});Q7=makeQuery(id+"F0.imprint","IMPRINT",FACE,{"disambiguationData":[TD([[makeQuery(id+"F0.imprint","IMPRINT",EDGE,{"disambiguationData":[TD([[subQ4,1.0]])],"derivedFrom":subQ3}),1.0]])]});}
            var Q8;
            {var subQ0=sQuery(id+"F0.wireOp",EDGE,"E33.trimOffspring");var subQ1=sQuery(id+"F0.wireOp",EDGE,"E15");var subQ2=makeQuery(id+"F0.imprint","INTERSECT",VERTEX,{"disambiguationData":[OD(0.0)],"derivedFrom":[subQ1,subQ0]});Q8=makeQuery(id+"F0.imprint","IMPRINT",FACE,{"disambiguationData":[TD([[makeQuery(id+"F0.imprint","IMPRINT",EDGE,{"disambiguationData":[TD([[subQ2,1.0]])],"derivedFrom":subQ1}),-1.0]])]});}
            var Q9;
            {var subQ1=sQuery(id+"F0.wireOp",EDGE,"E7");var subQ3=sQuery(id+"F0.wireOp",EDGE,"E31");var subQ4=makeQuery(id+"F0.imprint","INTERSECT",VERTEX,{"derivedFrom":[subQ1,subQ3]});Q9=makeQuery(id+"F0.imprint","IMPRINT",FACE,{"disambiguationData":[TD([[makeQuery(id+"F0.imprint","IMPRINT",EDGE,{"disambiguationData":[TD([[subQ4,-1.0]])],"derivedFrom":subQ3}),1.0]])]});}
            var Q10;
            {var subQ0=sQuery(id+"F0.wireOp",EDGE,"E33.trimOffspring");var subQ1=sQuery(id+"F0.wireOp",EDGE,"E30");var subQ2=makeQuery(id+"F0.imprint","INTERSECT",VERTEX,{"disambiguationData":[OD(0.0)],"derivedFrom":[subQ1,subQ0]});Q10=makeQuery(id+"F0.imprint","IMPRINT",FACE,{"disambiguationData":[TD([[makeQuery(id+"F0.imprint","IMPRINT",EDGE,{"disambiguationData":[TD([[subQ2,1.0]])],"derivedFrom":subQ1}),-1.0]])]});}
            var Q11;
            {var subQ0=sQuery(id+"F0.wireOp",EDGE,"E33.trimOffspring");var subQ1=sQuery(id+"F0.wireOp",EDGE,"E15");var subQ2=makeQuery(id+"F0.imprint","INTERSECT",VERTEX,{"disambiguationData":[OD(1.0)],"derivedFrom":[subQ1,subQ0]});Q11=makeQuery(id+"F0.imprint","IMPRINT",FACE,{"disambiguationData":[TD([[makeQuery(id+"F0.imprint","IMPRINT",EDGE,{"disambiguationData":[TD([[subQ2,-1.0]])],"derivedFrom":subQ1}),-1.0]])]});}
            var Q12;
            {var subQ0=sQuery(id+"F0.wireOp",EDGE,"E32.0");var subQ1=sQuery(id+"F0.wireOp",EDGE,"E25");var subQ2=makeQuery(id+"F0.imprint","INTERSECT",VERTEX,{"derivedFrom":[subQ1,subQ0]});Q12=makeQuery(id+"F0.imprint","IMPRINT",FACE,{"disambiguationData":[TD([[makeQuery(id+"F0.imprint","IMPRINT",EDGE,{"disambiguationData":[TD([[subQ2,1.0]])],"derivedFrom":subQ1}),-1.0]])]});}
            var Q13;
            {var subQ1=sQuery(id+"F0.wireOp",EDGE,"E3");var subQ3=sQuery(id+"F0.wireOp",EDGE,"E31");var subQ4=makeQuery(id+"F0.imprint","INTERSECT",VERTEX,{"derivedFrom":[subQ1,subQ3]});Q13=makeQuery(id+"F0.imprint","IMPRINT",FACE,{"disambiguationData":[TD([[makeQuery(id+"F0.imprint","IMPRINT",EDGE,{"disambiguationData":[TD([[subQ4,-1.0]])],"derivedFrom":subQ3}),1.0]])]});}
            var Q14;
            {var subQ1=sQuery(id+"F0.wireOp",EDGE,"E5");var subQ3=sQuery(id+"F0.wireOp",EDGE,"E32.0");var subQ4=makeQuery(id+"F0.imprint","INTERSECT",VERTEX,{"derivedFrom":[subQ1,subQ3]});Q14=makeQuery(id+"F0.imprint","IMPRINT",FACE,{"disambiguationData":[TD([[makeQuery(id+"F0.imprint","IMPRINT",EDGE,{"disambiguationData":[TD([[subQ4,1.0]])],"derivedFrom":subQ3}),1.0]])]});}
            var Q15;
            {var subQ1=sQuery(id+"F0.wireOp",EDGE,"E5");var subQ3=sQuery(id+"F0.wireOp",EDGE,"E33.trimOffspring");var subQ4=makeQuery(id+"F0.imprint","INTERSECT",VERTEX,{"derivedFrom":[subQ1,subQ3]});Q15=makeQuery(id+"F0.imprint","IMPRINT",FACE,{"disambiguationData":[TD([[makeQuery(id+"F0.imprint","IMPRINT",EDGE,{"disambiguationData":[TD([[subQ4,-1.0]])],"derivedFrom":subQ3}),-1.0]])]});}
            var Q16;
            {var subQ0=sQuery(id+"F0.wireOp",EDGE,"E33.trimOffspring");var subQ1=sQuery(id+"F0.wireOp",EDGE,"E30");var subQ2=makeQuery(id+"F0.imprint","INTERSECT",VERTEX,{"disambiguationData":[OD(1.0)],"derivedFrom":[subQ1,subQ0]});Q16=makeQuery(id+"F0.imprint","IMPRINT",FACE,{"disambiguationData":[TD([[makeQuery(id+"F0.imprint","IMPRINT",EDGE,{"disambiguationData":[TD([[subQ2,-1.0]])],"derivedFrom":subQ1}),-1.0]])]});}
            var Q17;
            {var subQ1=sQuery(id+"F0.wireOp",EDGE,"E7");var subQ3=sQuery(id+"F0.wireOp",EDGE,"E28");var subQ4=makeQuery(id+"F0.imprint","INTERSECT",VERTEX,{"derivedFrom":[subQ1,subQ3]});Q17=makeQuery(id+"F0.imprint","IMPRINT",FACE,{"disambiguationData":[TD([[makeQuery(id+"F0.imprint","IMPRINT",EDGE,{"disambiguationData":[TD([[subQ4,1.0]])],"derivedFrom":subQ3}),1.0]])]});}
            var Q18;
            {var subQ0=sQuery(id+"F0.wireOp",EDGE,"E33.trimOffspring");var subQ1=sQuery(id+"F0.wireOp",EDGE,"E28");var subQ2=makeQuery(id+"F0.imprint","INTERSECT",VERTEX,{"disambiguationData":[OD(1.0)],"derivedFrom":[subQ1,subQ0]});Q18=makeQuery(id+"F0.imprint","IMPRINT",FACE,{"disambiguationData":[TD([[makeQuery(id+"F0.imprint","IMPRINT",EDGE,{"disambiguationData":[TD([[subQ2,1.0]])],"derivedFrom":subQ1}),-1.0]])]});}
            var Q19;
            {var subQ1=sQuery(id+"F0.wireOp",EDGE,"E8");var subQ3=sQuery(id+"F0.wireOp",EDGE,"E28");var subQ4=makeQuery(id+"F0.imprint","INTERSECT",VERTEX,{"derivedFrom":[subQ1,subQ3]});Q19=makeQuery(id+"F0.imprint","IMPRINT",FACE,{"disambiguationData":[TD([[makeQuery(id+"F0.imprint","IMPRINT",EDGE,{"disambiguationData":[TD([[subQ4,-1.0]])],"derivedFrom":subQ3}),1.0]])]});}
            var Q20;
            {var subQ1=sQuery(id+"F0.wireOp",EDGE,"E8");var subQ3=sQuery(id+"F0.wireOp",EDGE,"E31");var subQ4=makeQuery(id+"F0.imprint","INTERSECT",VERTEX,{"derivedFrom":[subQ1,subQ3]});Q20=makeQuery(id+"F0.imprint","IMPRINT",FACE,{"disambiguationData":[TD([[makeQuery(id+"F0.imprint","IMPRINT",EDGE,{"disambiguationData":[TD([[subQ4,1.0]])],"derivedFrom":subQ3}),1.0]])]});}
            var Q21;
            {var subQ3=sQuery(id+"F0.wireOp",EDGE,"E28");var subQ5=sQuery(id+"F0.wireOp",EDGE,"E32.0");var subQ7=makeQuery(id+"F0.imprint","INTERSECT",VERTEX,{"disambiguationData":[OD(0.0)],"derivedFrom":[subQ3,subQ5]});Q21=makeQuery(id+"F0.imprint","IMPRINT",FACE,{"disambiguationData":[TD([[makeQuery(id+"F0.imprint","IMPRINT",EDGE,{"disambiguationData":[TD([[subQ7,-1.0]])],"derivedFrom":subQ3}),1.0]])]});}
            extrude(context, id + "F8", {"entities" : qUnion([Q0, Q1, Q2, Q3, Q4, Q5, Q6, Q7, Q8, Q9, Q10, Q11, Q12, Q13, Q14, Q15, Q16, Q17, Q18, Q19, Q20, Q21]), "endBound" : BoundingType.SYMMETRIC, "depth" : 355.6 * mm, "offsetDistance" : 25.4 * mm, "hasSecondDirection" : true, "secondDirectionOppositeDirection" : true, "secondDirectionDepth" : 237.82 * mm});
        }
        {
            var Q0;
            {var subQ0=sQuery(id+"F0.wireOp",EDGE,"E32.0");var subQ1=sQuery(id+"F0.wireOp",EDGE,"E9");var subQ2=makeQuery(id+"F0.imprint","INTERSECT",VERTEX,{"derivedFrom":[subQ1,subQ0]});Q0=makeQuery(id+"F0.imprint","IMPRINT",FACE,{"disambiguationData":[TD([[makeQuery(id+"F0.imprint","IMPRINT",EDGE,{"disambiguationData":[TD([[subQ2,-1.0]])],"derivedFrom":subQ1}),-1.0]])]});}
            var Q1;
            {var subQ0=sQuery(id+"F0.wireOp",EDGE,"E32.0");var subQ1=sQuery(id+"F0.wireOp",EDGE,"E9");var subQ2=makeQuery(id+"F0.imprint","INTERSECT",VERTEX,{"derivedFrom":[subQ1,subQ0]});Q1=makeQuery(id+"F0.imprint","IMPRINT",FACE,{"disambiguationData":[TD([[makeQuery(id+"F0.imprint","IMPRINT",EDGE,{"disambiguationData":[TD([[subQ2,-1.0]])],"derivedFrom":subQ1}),1.0]])]});}
            var Q2;
            {var subQ1=sQuery(id+"F0.wireOp",EDGE,"E9");var subQ3=sQuery(id+"F0.wireOp",EDGE,"E32.0");var subQ4=makeQuery(id+"F0.imprint","INTERSECT",VERTEX,{"derivedFrom":[subQ1,subQ3]});Q2=makeQuery(id+"F0.imprint","IMPRINT",FACE,{"disambiguationData":[TD([[makeQuery(id+"F0.imprint","IMPRINT",EDGE,{"disambiguationData":[TD([[subQ4,1.0]])],"derivedFrom":subQ3}),1.0]])]});}
            var Q3;
            {var subQ1=sQuery(id+"F0.wireOp",EDGE,"E9");var subQ3=sQuery(id+"F0.wireOp",EDGE,"E33.trimOffspring");var subQ4=makeQuery(id+"F0.imprint","INTERSECT",VERTEX,{"derivedFrom":[subQ1,subQ3]});Q3=makeQuery(id+"F0.imprint","IMPRINT",FACE,{"disambiguationData":[TD([[makeQuery(id+"F0.imprint","IMPRINT",EDGE,{"disambiguationData":[TD([[subQ4,1.0]])],"derivedFrom":subQ3}),-1.0]])]});}
            var Q4;
            {var subQ1=sQuery(id+"F0.wireOp",EDGE,"E9");var subQ3=sQuery(id+"F0.wireOp",EDGE,"E33.trimOffspring");var subQ4=makeQuery(id+"F0.imprint","INTERSECT",VERTEX,{"derivedFrom":[subQ1,subQ3]});Q4=makeQuery(id+"F0.imprint","IMPRINT",FACE,{"disambiguationData":[TD([[makeQuery(id+"F0.imprint","IMPRINT",EDGE,{"disambiguationData":[TD([[subQ4,-1.0]])],"derivedFrom":subQ3}),-1.0]])]});}
            var Q5;
            {var subQ1=sQuery(id+"F0.wireOp",EDGE,"E9");var subQ3=sQuery(id+"F0.wireOp",EDGE,"E32.0");var subQ4=makeQuery(id+"F0.imprint","INTERSECT",VERTEX,{"derivedFrom":[subQ1,subQ3]});Q5=makeQuery(id+"F0.imprint","IMPRINT",FACE,{"disambiguationData":[TD([[makeQuery(id+"F0.imprint","IMPRINT",EDGE,{"disambiguationData":[TD([[subQ4,-1.0]])],"derivedFrom":subQ3}),1.0]])]});}
            extrude(context, id + "F9", {"entities" : qUnion([Q0, Q1, Q2, Q3, Q4, Q5]), "operationType" : NewBodyOperationType.ADD, "endBound" : BoundingType.SYMMETRIC, "depth" : 406.4 * mm, "offsetDistance" : 25.4 * mm});
        }
        {
            var Q0;
            {var subQ0=sQuery(id+"F0.wireOp",EDGE,"E27");var subQ1=sQuery(id+"F0.wireOp",EDGE,"E19");var subQ2=makeQuery(id+"F0.imprint","INTERSECT",VERTEX,{"derivedFrom":[subQ1,subQ0]});Q0=makeQuery(id+"F0.imprint","IMPRINT",FACE,{"disambiguationData":[TD([[makeQuery(id+"F0.imprint","IMPRINT",EDGE,{"disambiguationData":[TD([[subQ2,-1.0]])],"derivedFrom":subQ1}),-1.0]])]});}
            var Q1;
            {var subQ3=sQuery(id+"F0.wireOp",EDGE,"E11");var subQ5=sQuery(id+"F0.wireOp",EDGE,"E10");var subQ6=makeQuery(id+"F0.imprint","INTERSECT",VERTEX,{"derivedFrom":[subQ5,subQ3]});Q1=makeQuery(id+"F0.imprint","IMPRINT",FACE,{"disambiguationData":[TD([[makeQuery(id+"F0.imprint","IMPRINT",EDGE,{"disambiguationData":[TD([[subQ6,1.0]])],"derivedFrom":subQ3}),-1.0]])]});}
            var Q2;
            {var subQ3=sQuery(id+"F0.wireOp",EDGE,"E12");var subQ6=sQuery(id+"F0.wireOp",EDGE,"E10");var subQ9=makeQuery(id+"F0.imprint","INTERSECT",VERTEX,{"derivedFrom":[subQ6,subQ3]});Q2=makeQuery(id+"F0.imprint","IMPRINT",FACE,{"disambiguationData":[TD([[makeQuery(id+"F0.imprint","IMPRINT",EDGE,{"disambiguationData":[TD([[subQ9,-1.0]])],"derivedFrom":subQ3}),-1.0]])]});}
            var Q3;
            {var subQ1=sQuery(id+"F0.wireOp",EDGE,"E13");var subQ3=sQuery(id+"F0.wireOp",EDGE,"E26");var subQ4=makeQuery(id+"F0.imprint","INTERSECT",VERTEX,{"derivedFrom":[subQ1,subQ3]});Q3=makeQuery(id+"F0.imprint","IMPRINT",FACE,{"disambiguationData":[TD([[makeQuery(id+"F0.imprint","IMPRINT",EDGE,{"disambiguationData":[TD([[subQ4,1.0]])],"derivedFrom":subQ3}),1.0]])]});}
            var Q4;
            {var subQ0=sQuery(id+"F0.wireOp",EDGE,"E20");var subQ1=sQuery(id+"F0.wireOp",EDGE,"E18");var subQ2=makeQuery(id+"F0.imprint","INTERSECT",VERTEX,{"derivedFrom":[subQ1,subQ0]});Q4=makeQuery(id+"F0.imprint","IMPRINT",FACE,{"disambiguationData":[TD([[makeQuery(id+"F0.imprint","IMPRINT",EDGE,{"disambiguationData":[TD([[subQ2,-1.0]])],"derivedFrom":subQ1}),-1.0]])]});}
            var Q5;
            {var subQ0=sQuery(id+"F0.wireOp",EDGE,"E26");var subQ1=sQuery(id+"F0.wireOp",EDGE,"E12");var subQ2=makeQuery(id+"F0.imprint","INTERSECT",VERTEX,{"derivedFrom":[subQ1,subQ0]});Q5=makeQuery(id+"F0.imprint","IMPRINT",FACE,{"disambiguationData":[TD([[makeQuery(id+"F0.imprint","IMPRINT",EDGE,{"disambiguationData":[TD([[subQ2,1.0]])],"derivedFrom":subQ1}),-1.0]])]});}
            var Q6;
            {var subQ0=sQuery(id+"F0.wireOp",EDGE,"E27");var subQ1=sQuery(id+"F0.wireOp",EDGE,"E19");var subQ2=makeQuery(id+"F0.imprint","INTERSECT",VERTEX,{"derivedFrom":[subQ1,subQ0]});Q6=makeQuery(id+"F0.imprint","IMPRINT",FACE,{"disambiguationData":[TD([[makeQuery(id+"F0.imprint","IMPRINT",EDGE,{"disambiguationData":[TD([[subQ2,1.0]])],"derivedFrom":subQ1}),1.0]])]});}
            var Q7;
            {var subQ0=sQuery(id+"F0.wireOp",EDGE,"E22");var subQ1=sQuery(id+"F0.wireOp",EDGE,"E21");var subQ2=makeQuery(id+"F0.imprint","INTERSECT",VERTEX,{"derivedFrom":[subQ1,subQ0]});Q7=makeQuery(id+"F0.imprint","IMPRINT",FACE,{"disambiguationData":[TD([[makeQuery(id+"F0.imprint","IMPRINT",EDGE,{"disambiguationData":[TD([[subQ2,1.0]])],"derivedFrom":subQ1}),-1.0]])]});}
            var Q8;
            {var subQ0=sQuery(id+"F0.wireOp",EDGE,"E29");var subQ1=sQuery(id+"F0.wireOp",EDGE,"E22");var subQ2=makeQuery(id+"F0.imprint","INTERSECT",VERTEX,{"derivedFrom":[subQ1,subQ0]});Q8=makeQuery(id+"F0.imprint","IMPRINT",FACE,{"disambiguationData":[TD([[makeQuery(id+"F0.imprint","IMPRINT",EDGE,{"disambiguationData":[TD([[subQ2,-1.0]])],"derivedFrom":subQ1}),1.0]])]});}
            var Q9;
            {var subQ0=sQuery(id+"F0.wireOp",EDGE,"E12");var subQ1=sQuery(id+"F0.wireOp",EDGE,"E10");var subQ2=makeQuery(id+"F0.imprint","INTERSECT",VERTEX,{"derivedFrom":[subQ1,subQ0]});Q9=makeQuery(id+"F0.imprint","IMPRINT",FACE,{"disambiguationData":[TD([[makeQuery(id+"F0.imprint","IMPRINT",EDGE,{"disambiguationData":[TD([[subQ2,-1.0]])],"derivedFrom":subQ0}),1.0]])]});}
            var Q10;
            {var subQ0=sQuery(id+"F0.wireOp",EDGE,"E11");var subQ1=sQuery(id+"F0.wireOp",EDGE,"E10");var subQ2=makeQuery(id+"F0.imprint","INTERSECT",VERTEX,{"derivedFrom":[subQ1,subQ0]});Q10=makeQuery(id+"F0.imprint","IMPRINT",FACE,{"disambiguationData":[TD([[makeQuery(id+"F0.imprint","IMPRINT",EDGE,{"disambiguationData":[TD([[subQ2,1.0]])],"derivedFrom":subQ0}),1.0]])]});}
            var Q11;
            {var subQ0=sQuery(id+"F0.wireOp",EDGE,"E20");var subQ1=sQuery(id+"F0.wireOp",EDGE,"E18");var subQ2=makeQuery(id+"F0.imprint","INTERSECT",VERTEX,{"derivedFrom":[subQ1,subQ0]});Q11=makeQuery(id+"F0.imprint","IMPRINT",FACE,{"disambiguationData":[TD([[makeQuery(id+"F0.imprint","IMPRINT",EDGE,{"disambiguationData":[TD([[subQ2,1.0]])],"derivedFrom":subQ1}),-1.0]])]});}
            var Q12;
            {var subQ3=sQuery(id+"F0.wireOp",EDGE,"E11");var subQ7=sQuery(id+"F0.wireOp",EDGE,"E26");var subQ9=makeQuery(id+"F0.imprint","INTERSECT",VERTEX,{"derivedFrom":[subQ3,subQ7]});Q12=makeQuery(id+"F0.imprint","IMPRINT",FACE,{"disambiguationData":[TD([[makeQuery(id+"F0.imprint","IMPRINT",EDGE,{"disambiguationData":[TD([[subQ9,-1.0]])],"derivedFrom":subQ3}),1.0]])]});}
            var Q13;
            {var subQ1=sQuery(id+"F0.wireOp",EDGE,"E18");var subQ7=sQuery(id+"F0.wireOp",EDGE,"E19");var subQ9=makeQuery(id+"F0.imprint","INTERSECT",VERTEX,{"derivedFrom":[subQ1,subQ7]});Q13=makeQuery(id+"F0.imprint","IMPRINT",FACE,{"disambiguationData":[TD([[makeQuery(id+"F0.imprint","IMPRINT",EDGE,{"disambiguationData":[TD([[subQ9,-1.0]])],"derivedFrom":subQ1}),-1.0]])]});}
            var Q14;
            {var subQ0=sQuery(id+"F0.wireOp",EDGE,"E26");var subQ1=sQuery(id+"F0.wireOp",EDGE,"E11");var subQ2=makeQuery(id+"F0.imprint","INTERSECT",VERTEX,{"derivedFrom":[subQ1,subQ0]});Q14=makeQuery(id+"F0.imprint","IMPRINT",FACE,{"disambiguationData":[TD([[makeQuery(id+"F0.imprint","IMPRINT",EDGE,{"disambiguationData":[TD([[subQ2,-1.0]])],"derivedFrom":subQ1}),-1.0]])]});}
            var Q15;
            {var subQ0=sQuery(id+"F0.wireOp",EDGE,"E22");var subQ1=sQuery(id+"F0.wireOp",EDGE,"E21");var subQ2=makeQuery(id+"F0.imprint","INTERSECT",VERTEX,{"derivedFrom":[subQ1,subQ0]});Q15=makeQuery(id+"F0.imprint","IMPRINT",FACE,{"disambiguationData":[TD([[makeQuery(id+"F0.imprint","IMPRINT",EDGE,{"disambiguationData":[TD([[subQ2,-1.0]])],"derivedFrom":subQ1}),-1.0]])]});}
            var Q16;
            {var subQ0=sQuery(id+"F0.wireOp",EDGE,"E19");var subQ1=sQuery(id+"F0.wireOp",EDGE,"E18");var subQ2=makeQuery(id+"F0.imprint","INTERSECT",VERTEX,{"derivedFrom":[subQ1,subQ0]});Q16=makeQuery(id+"F0.imprint","IMPRINT",FACE,{"disambiguationData":[TD([[makeQuery(id+"F0.imprint","IMPRINT",EDGE,{"disambiguationData":[TD([[subQ2,1.0]])],"derivedFrom":subQ1}),-1.0]])]});}
            extrude(context, id + "F10", {"entities" : qUnion([Q0, Q1, Q2, Q3, Q4, Q5, Q6, Q7, Q8, Q9, Q10, Q11, Q12, Q13, Q14, Q15, Q16]), "oppositeDirection" : true, "depth" : 203.2 * mm, "offsetDistance" : 25.4 * mm, "hasSecondDirection" : true, "secondDirectionOppositeDirection" : true, "secondDirectionDepth" : 177.8 * mm});
        }
    });
